# Revit family: Shower-Receptor-STERLING-GUARD-95081_1
name_source: partatom
category: Plumbing Fixtures
revit_build: Autodesk Revit 2017 (Build: 20160225_1515(x64)
units: mm (PartAtom-declared; Revit-internal decimal feet)

## family parameters
Cut with Voids When Loaded = No
Host = Face
OmniClass Number = 23.31.17.13
OmniClass Title = Shower Receptors
Part Type = Normal
Room Calculation Point = No
Round Connector Dimension = Use Diameter
Shared = No

## types (1)
- 0-White
    ADA Compliant = No
    Assembly Code = D2010700
    CW Connection = No
    Cold Water Inlet = Cold Water Inlet
    Date Modified = 12/10/2020
    Default Elevation = 0"
    Description = 60 inch x 42 inch shower base
    Drain Included = No
    Finish = STERLING-Acrylic-0-White
    Flow Rate = 0 GPM
    HW Connection = No
    Height = 4 3/16"
    Hot Water Inlet = Hot Water Inlet
    Length = 60"
    Manufacturer = STERLING Co.
    Master Format 2014 = 22 41 23
    Master Format 2014 Name = Residential Showers
    Material = Acrylic
    Model = 95081-0
    Pressure = 0.00 psi
    Product Documentation Link = https://resources.kohler.com
    Product Name = GUARD
    Product Page URL = http://www.sterlingplumbing.com
    Type = 1
    URL = https://www.sterlingplumbing.com
    Vent Connection = No
    Waste Connection = Yes
    Waste Water Outlet = Waste Water Outlet
    WaterSense Certified = No
    Width = 42"

## geometry (parser evidence)
native form markers: Sweep x5
no freeform markers — native parametric forms only
